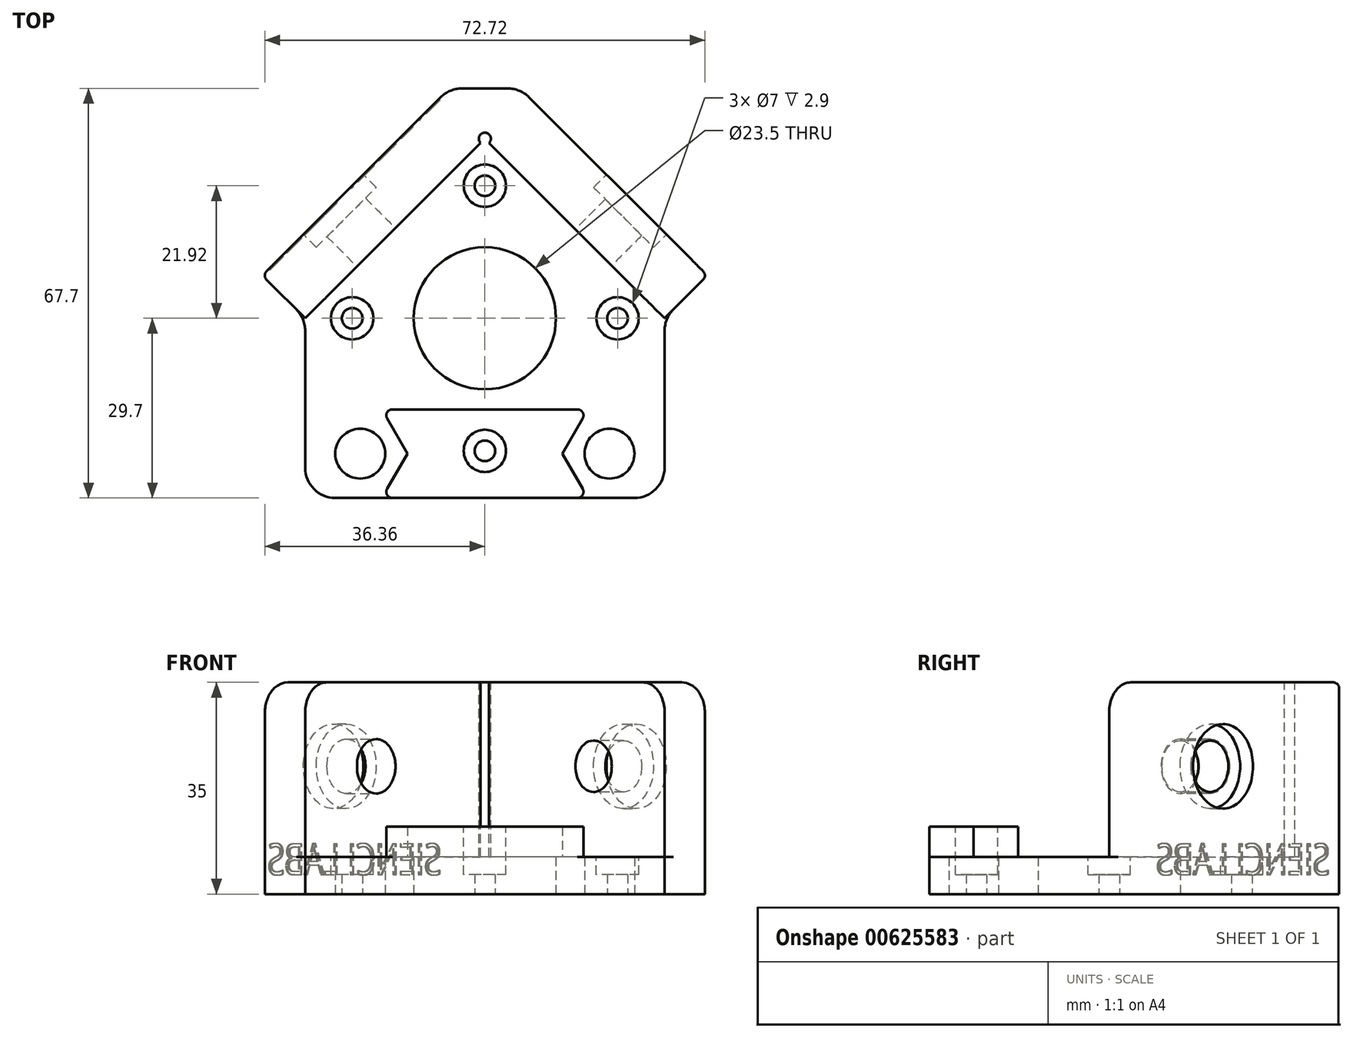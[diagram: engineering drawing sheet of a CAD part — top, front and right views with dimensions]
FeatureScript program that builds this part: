
annotation { "Feature Type Name" : "Feature", "Feature Type Description" : "" }
export const myFeature = defineFeature(function(context is Context, id is Id, definition is map)
    precondition{}
    {
        {
            var Q0;
            Q0=qCreatedBy(makeId("Top.planeOp"),FACE);
            var sketch = newSketch(context, id + "F0", { "sketchPlane" : qUnion([Q0])});
            skLineSegment(sketch, "E0", {"start": v(0, 0) * mm, "end": v(-29.7, 0) * mm});
            skLineSegment(sketch, "E1", {"start": v(-29.7, 0) * mm, "end": v(-29.7, 29.7) * mm});
            skLineSegment(sketch, "E2", {"start": v(-29.7, 29.7) * mm, "end": v(0, 59.4) * mm});
            skLineSegment(sketch, "E3", {"start": v(0, 59.4) * mm, "end": v(0, 0) * mm, "construction": true});
            skLineSegment(sketch, "E4", {"start": v(-29.7, 7.78) * mm, "end": v(0, 7.78) * mm, "construction": true});
            skCircle(sketch, "E5", {"center": v(0, 29.7) * mm, "radius": 11.75 * mm});
            skLineSegment(sketch, "E6", {"start": v(0, 29.7) * mm, "end": v(0, 59.4) * mm, "construction": true});
            skLineSegment(sketch, "E7", {"start": v(0, 59.4) * mm, "end": v(-29.7, 29.7) * mm, "construction": true});
            skLineSegment(sketch, "E8", {"start": v(-29.7, 29.7) * mm, "end": v(0, 0) * mm, "construction": true});
            skLineSegment(sketch, "E9", {"start": v(0, 51.62) * mm, "end": v(-21.92, 29.7) * mm, "construction": true});
            skLineSegment(sketch, "E10", {"start": v(-21.92, 29.7) * mm, "end": v(0, 7.78) * mm, "construction": true});
            skCircle(sketch, "E11", {"center": v(-20.59, 7.32) * mm, "radius": 4.12 * mm});
            skCircle(sketch, "E12", {"center": v(-21.92, 29.7) * mm, "radius": 1.7 * mm});
            skCircle(sketch, "E13", {"center": v(0, 51.62) * mm, "radius": 1.7 * mm});
            skCircle(sketch, "E14", {"center": v(0, 7.78) * mm, "radius": 1.7 * mm});
            skLineSegment(sketch, "E15.MirrorCS", {"start": v(29.7, 29.7) * mm, "end": v(0, 59.4) * mm});
            skLineSegment(sketch, "E16.MirrorCS", {"start": v(0, 0) * mm, "end": v(29.7, 0) * mm});
            skLineSegment(sketch, "E17.MirrorCS", {"start": v(29.7, 0) * mm, "end": v(29.7, 29.7) * mm});
            skLineSegment(sketch, "E18.MirrorCS", {"start": v(29.7, 7.78) * mm, "end": v(0, 7.78) * mm, "construction": true});
            skCircle(sketch, "E19.MirrorC", {"center": v(21.92, 29.7) * mm, "radius": 1.7 * mm});
            skCircle(sketch, "E20.MirrorC", {"center": v(20.6, 7.32) * mm, "radius": 4.12 * mm});
            skLineSegment(sketch, "E21.MirrorCS", {"start": v(0, 59.4) * mm, "end": v(29.7, 29.7) * mm, "construction": true});
            skLineSegment(sketch, "E22.MirrorCS", {"start": v(0, 51.62) * mm, "end": v(21.92, 29.7) * mm, "construction": true});
            skLineSegment(sketch, "E23.MirrorCS", {"start": v(21.92, 29.7) * mm, "end": v(0, 7.78) * mm, "construction": true});
            skLineSegment(sketch, "E24.MirrorCS", {"start": v(29.7, 29.7) * mm, "end": v(0, 0) * mm, "construction": true});
            skSolve(sketch);
        }
        {
            var Q0;
            Q0=qSketchRegion(id+"F0",true);
            extrude(context, id + "F1", {"entities" : qUnion([Q0]), "depth" : 6.13 * mm, "offsetDistance" : 25 * mm});
        }
        {
            var Q0;
            Q0=makeQuery(id+"F1.opExtrude","CAP_FACE",FACE,{"disambiguationData":[OSD([sQuery(id+"F0.wireOp",EDGE,"E0"),sQuery(id+"F0.wireOp",EDGE,"E1"),sQuery(id+"F0.wireOp",EDGE,"E2"),sQuery(id+"F0.wireOp",EDGE,"E5"),sQuery(id+"F0.wireOp",EDGE,"E11"),sQuery(id+"F0.wireOp",EDGE,"E12"),sQuery(id+"F0.wireOp",EDGE,"E15.MirrorCS"),sQuery(id+"F0.wireOp",EDGE,"E16.MirrorCS"),sQuery(id+"F0.wireOp",EDGE,"E17.MirrorCS"),sQuery(id+"F0.wireOp",EDGE,"E14"),sQuery(id+"F0.wireOp",EDGE,"E13"),sQuery(id+"F0.wireOp",EDGE,"E19.MirrorC"),sQuery(id+"F0.wireOp",EDGE,"E20.MirrorC")])],"isStart":true});
            var sketch = newSketch(context, id + "F2", { "sketchPlane" : qUnion([Q0])});
            skLineSegment(sketch, "E25", {"start": v(-29.7, -29.7) * mm, "end": v(-36.77, -36.77) * mm});
            skLineSegment(sketch, "E26", {"start": v(-36.77, -36.77) * mm, "end": v(-5.84, -67.7) * mm});
            skLineSegment(sketch, "E27", {"start": v(-5.84, -67.7) * mm, "end": v(0, -67.7) * mm});
            skLineSegment(sketch, "E28", {"start": v(0, -29.7) * mm, "end": v(-11.75, -29.7) * mm, "construction": true});
            skLineSegment(sketch, "E29", {"start": v(0, -67.7) * mm, "end": v(0, -29.7) * mm, "construction": true});
            skLineSegment(sketch, "E30.MirrorCS", {"start": v(0, -29.7) * mm, "end": v(11.75, -29.7) * mm, "construction": true});
            skLineSegment(sketch, "E31.MirrorCS", {"start": v(5.84, -67.7) * mm, "end": v(0, -67.7) * mm});
            skLineSegment(sketch, "E32.MirrorCS", {"start": v(36.77, -36.77) * mm, "end": v(5.84, -67.7) * mm});
            skLineSegment(sketch, "E33.MirrorCS", {"start": v(29.7, -29.7) * mm, "end": v(36.77, -36.77) * mm});
            skLineSegment(sketch, "E34", {"start": v(-29.7, -29.7) * mm, "end": v(0, -59.4) * mm});
            skLineSegment(sketch, "E35", {"start": v(0, -59.4) * mm, "end": v(29.7, -29.7) * mm});
            skSolve(sketch);
        }
        {
            var Q0;
            Q0=qSketchRegion(id+"F2",true);
            extrude(context, id + "F3", {"entities" : qUnion([Q0]), "operationType" : NewBodyOperationType.ADD, "oppositeDirection" : true, "depth" : 35 * mm, "offsetDistance" : 25 * mm});
        }
        {
            var Q0;
            Q0=makeQuery(id+"F3.opExtrude","SWEPT_FACE",FACE,{"disambiguationData":[OSD([sQuery(id+"F2.wireOp",EDGE,"E34")])]});
            var sketch = newSketch(context, id + "F4", { "sketchPlane" : qUnion([Q0])});
            skCircle(sketch, "E36", {"center": v(16.6, 21.13) * mm, "radius": 4.5 * mm});
            skLineSegment(sketch, "E37", {"start": v(42, 6.13) * mm, "end": v(-8.8, 6.13) * mm, "construction": true});
            skLineSegment(sketch, "E38", {"start": v(16.6, 6.13) * mm, "end": v(16.6, 35) * mm, "construction": true});
            skSolve(sketch);
        }
        {
            var Q0;
            Q0=qSketchRegion(id+"F4",true);
            extrude(context, id + "F5", {"entities" : qUnion([Q0]), "operationType" : NewBodyOperationType.REMOVE, "endBound" : BoundingType.UP_TO_NEXT, "oppositeDirection" : true, "depth" : 25 * mm, "offsetDistance" : 25 * mm});
        }
        {
            var Q0;
            Q0=makeQuery(id+"F3.opExtrude","SWEPT_FACE",FACE,{"disambiguationData":[OSD([sQuery(id+"F2.wireOp",EDGE,"E35")])]});
            var sketch = newSketch(context, id + "F6", { "sketchPlane" : qUnion([Q0])});
            skLineSegment(sketch, "E39", {"start": v(-42, 6.13) * mm, "end": v(8.8, 6.13) * mm, "construction": true});
            skLineSegment(sketch, "E40", {"start": v(-16.6, 6.13) * mm, "end": v(-16.6, 35) * mm, "construction": true});
            skCircle(sketch, "E41", {"center": v(-16.6, 21.13) * mm, "radius": 4.25 * mm});
            skSolve(sketch);
        }
        {
            var Q0;
            Q0=qSketchRegion(id+"F6",true);
            extrude(context, id + "F7", {"entities" : qUnion([Q0]), "operationType" : NewBodyOperationType.REMOVE, "endBound" : BoundingType.UP_TO_NEXT, "oppositeDirection" : true, "depth" : 25 * mm, "offsetDistance" : 25 * mm});
        }
        {
            var Q0;
            Q0=makeQuery(id+"F3.opExtrude","SWEPT_FACE",FACE,{"disambiguationData":[OSD([sQuery(id+"F2.wireOp",EDGE,"E26")])]});
            var sketch = newSketch(context, id + "F8", { "sketchPlane" : qUnion([Q0])});
            skCircle(sketch, "E42", {"center": v(-16.6, 21.13) * mm, "radius": 7 * mm});
            skSolve(sketch);
        }
        {
            var Q0;
            Q0=qSketchRegion(id+"F8",true);
            extrude(context, id + "F9", {"entities" : qUnion([Q0]), "operationType" : NewBodyOperationType.REMOVE, "oppositeDirection" : true, "depth" : 3 * mm, "offsetDistance" : 25 * mm});
        }
        {
            var Q0;
            Q0=makeQuery(id+"F3.opExtrude","SWEPT_FACE",FACE,{"disambiguationData":[OSD([sQuery(id+"F2.wireOp",EDGE,"E32.MirrorCS")])]});
            var sketch = newSketch(context, id + "F10", { "sketchPlane" : qUnion([Q0])});
            skCircle(sketch, "E43", {"center": v(16.6, 21.13) * mm, "radius": 7 * mm});
            skSolve(sketch);
        }
        {
            var Q0;
            Q0=qSketchRegion(id+"F10",true);
            extrude(context, id + "F11", {"entities" : qUnion([Q0]), "operationType" : NewBodyOperationType.REMOVE, "oppositeDirection" : true, "depth" : 3 * mm, "offsetDistance" : 25 * mm});
        }
        {
            var Q0;
            Q0=makeQuery(id+"F1.opExtrude","CAP_FACE",FACE,{"disambiguationData":[OSD([sQuery(id+"F0.wireOp",EDGE,"E0"),sQuery(id+"F0.wireOp",EDGE,"E1"),sQuery(id+"F0.wireOp",EDGE,"E2"),sQuery(id+"F0.wireOp",EDGE,"E5"),sQuery(id+"F0.wireOp",EDGE,"E11"),sQuery(id+"F0.wireOp",EDGE,"E12"),sQuery(id+"F0.wireOp",EDGE,"E15.MirrorCS"),sQuery(id+"F0.wireOp",EDGE,"E16.MirrorCS"),sQuery(id+"F0.wireOp",EDGE,"E17.MirrorCS"),sQuery(id+"F0.wireOp",EDGE,"E14"),sQuery(id+"F0.wireOp",EDGE,"E13"),sQuery(id+"F0.wireOp",EDGE,"E19.MirrorC"),sQuery(id+"F0.wireOp",EDGE,"E20.MirrorC")])],"isStart":false});
            var sketch = newSketch(context, id + "F12", { "sketchPlane" : qUnion([Q0])});
            skCircle(sketch, "E44", {"center": v(0, 51.62) * mm, "radius": 3.5 * mm});
            skCircle(sketch, "E45", {"center": v(-21.92, 29.7) * mm, "radius": 3.5 * mm});
            skCircle(sketch, "E46", {"center": v(21.92, 29.7) * mm, "radius": 3.5 * mm});
            skCircle(sketch, "E47", {"center": v(0, 7.78) * mm, "radius": 3.5 * mm});
            skSolve(sketch);
        }
        {
            var Q0;
            Q0=makeQuery(id+"F3.opExtrude","CAP_EDGE",EDGE,{"disambiguationData":[OSD([sQuery(id+"F2.wireOp",EDGE,"E33.MirrorCS")])],"isStart":false});
            var Q1;
            Q1=makeQuery(id+"F3.opExtrude","CAP_EDGE",EDGE,{"disambiguationData":[OSD([sQuery(id+"F2.wireOp",EDGE,"E25")])],"isStart":false});
            var Q2;
            {var subQ0=sQuery(id+"F0.wireOp",EDGE,"E17.MirrorCS");Q2=makeQuery(id+"F3.boolean.opBoolean","MERGE",EDGE,{"derivedFrom":[makeQuery(id+"F1.opExtrude","SWEPT_EDGE",EDGE,{"disambiguationData":[OSD([sQuery(id+"F0.wireOp",EDGE,"E15.MirrorCS"),subQ0])]}),makeQuery(id+"F3.opExtrude","SWEPT_EDGE",EDGE,{"disambiguationData":[OSD([subQ0,sQuery(id+"F2.wireOp",EDGE,"E33.MirrorCS"),sQuery(id+"F2.wireOp",EDGE,"E35")])]})]});}
            var Q3;
            Q3=makeQuery(id+"F1.opExtrude","SWEPT_EDGE",EDGE,{"disambiguationData":[OSD([sQuery(id+"F0.wireOp",EDGE,"E16.MirrorCS"),sQuery(id+"F0.wireOp",EDGE,"E17.MirrorCS")])]});
            var Q4;
            Q4=makeQuery(id+"F1.opExtrude","SWEPT_EDGE",EDGE,{"disambiguationData":[OSD([sQuery(id+"F0.wireOp",EDGE,"E0"),sQuery(id+"F0.wireOp",EDGE,"E1")])]});
            var Q5;
            {var subQ0=sQuery(id+"F0.wireOp",EDGE,"E1");Q5=makeQuery(id+"F3.boolean.opBoolean","MERGE",EDGE,{"derivedFrom":[makeQuery(id+"F1.opExtrude","SWEPT_EDGE",EDGE,{"disambiguationData":[OSD([subQ0,sQuery(id+"F0.wireOp",EDGE,"E2")])]}),makeQuery(id+"F3.opExtrude","SWEPT_EDGE",EDGE,{"disambiguationData":[OSD([subQ0,sQuery(id+"F2.wireOp",EDGE,"E25"),sQuery(id+"F2.wireOp",EDGE,"E34")])]})]});}
            var Q6;
            Q6=makeQuery(id+"F3.opExtrude","SWEPT_EDGE",EDGE,{"disambiguationData":[OSD([sQuery(id+"F2.wireOp",EDGE,"E26"),sQuery(id+"F2.wireOp",EDGE,"E27")])]});
            var Q7;
            Q7=makeQuery(id+"F3.opExtrude","SWEPT_EDGE",EDGE,{"disambiguationData":[OSD([sQuery(id+"F2.wireOp",EDGE,"E31.MirrorCS"),sQuery(id+"F2.wireOp",EDGE,"E32.MirrorCS")])]});
            fillet(context, id + "F13", {"entities" : qUnion([Q0, Q1, Q2, Q3, Q4, Q5, Q6, Q7]), "radius" : 5 * mm, "tangentPropagation" : true, "allowEdgeOverflow" : false});
        }
        {
            var Q0;
            Q0=qSketchRegion(id+"F12",true);
            extrude(context, id + "F14", {"entities" : qUnion([Q0]), "operationType" : NewBodyOperationType.REMOVE, "oppositeDirection" : true, "depth" : 2.9 * mm, "offsetDistance" : 25 * mm});
        }
        {
            var Q0;
            Q0=makeQuery(id+"F3.opExtrude","SWEPT_FACE",FACE,{"disambiguationData":[OSD([sQuery(id+"F2.wireOp",EDGE,"E26")])]});
            var sketch = newSketch(context, id + "F15", { "sketchPlane" : qUnion([Q0])});
            skText(sketch, "E48", { "text": "SIENCI LABS\n", "fontName": "OpenSans-Regular.ttf"});
            const initialGuessF15  = {"E48": [-0.04167, 0.0032, 1, 0, 0.00516]};
            skSetInitialGuess(sketch, initialGuessF15);
            skSolve(sketch);
        }
        {
            var Q0;
            Q0=qSketchRegion(id+"F15",true);
            extrude(context, id + "F16", {"entities" : qUnion([Q0]), "operationType" : NewBodyOperationType.REMOVE, "oppositeDirection" : true, "depth" : 0.25 * mm, "offsetDistance" : 25 * mm});
        }
        {
            var Q0;
            Q0=makeQuery(id+"F1.opExtrude","CAP_FACE",FACE,{"disambiguationData":[OSD([sQuery(id+"F0.wireOp",EDGE,"E0"),sQuery(id+"F0.wireOp",EDGE,"E1"),sQuery(id+"F0.wireOp",EDGE,"E2"),sQuery(id+"F0.wireOp",EDGE,"E5"),sQuery(id+"F0.wireOp",EDGE,"E11"),sQuery(id+"F0.wireOp",EDGE,"E12"),sQuery(id+"F0.wireOp",EDGE,"E15.MirrorCS"),sQuery(id+"F0.wireOp",EDGE,"E16.MirrorCS"),sQuery(id+"F0.wireOp",EDGE,"E17.MirrorCS"),sQuery(id+"F0.wireOp",EDGE,"E14"),sQuery(id+"F0.wireOp",EDGE,"E13"),sQuery(id+"F0.wireOp",EDGE,"E19.MirrorC"),sQuery(id+"F0.wireOp",EDGE,"E20.MirrorC")])],"isStart":false});
            var sketch = newSketch(context, id + "F17", { "sketchPlane" : qUnion([Q0])});
            skCircle(sketch, "E49.cCircle", {"center": v(-20.59, 7.32) * mm, "radius": 6.75 * mm, "construction": true});
            skLineSegment(sketch, "E49.0", {"start": v(-16.7, 14.07) * mm, "end": v(-12.8, 7.32) * mm});
            skLineSegment(sketch, "E49.1", {"start": v(-12.8, 7.32) * mm, "end": v(-16.7, 0.57) * mm});
            skLineSegment(sketch, "E49.2", {"start": v(-16.7, 0.57) * mm, "end": v(-24.49, 0.57) * mm});
            skLineSegment(sketch, "E49.3", {"start": v(-24.49, 0.57) * mm, "end": v(-28.38, 7.32) * mm});
            skLineSegment(sketch, "E49.4", {"start": v(-28.38, 7.32) * mm, "end": v(-24.49, 14.07) * mm});
            skLineSegment(sketch, "E49.5", {"start": v(-24.49, 14.07) * mm, "end": v(-16.7, 14.07) * mm});
            skPoint(sketch, "E49.0.midPoint", {"position": v(-14.74, 10.7) * mm});
            skLineSegment(sketch, "E50", {"start": v(0, 59.4) * mm, "end": v(0, 0) * mm, "construction": true});
            skLineSegment(sketch, "E51.MirrorCS", {"start": v(24.49, 14.07) * mm, "end": v(16.7, 14.07) * mm});
            skLineSegment(sketch, "E52.MirrorCS", {"start": v(16.7, 14.07) * mm, "end": v(12.8, 7.32) * mm});
            skLineSegment(sketch, "E53.MirrorCS", {"start": v(28.38, 7.32) * mm, "end": v(24.49, 14.07) * mm});
            skCircle(sketch, "E54.MirrorC", {"center": v(20.59, 7.32) * mm, "radius": 6.75 * mm, "construction": true});
            skLineSegment(sketch, "E55.MirrorCS", {"start": v(24.49, 0.57) * mm, "end": v(28.38, 7.32) * mm});
            skLineSegment(sketch, "E56.MirrorCS", {"start": v(12.8, 7.32) * mm, "end": v(16.7, 0.57) * mm});
            skLineSegment(sketch, "E57.MirrorCS", {"start": v(16.7, 0.57) * mm, "end": v(24.49, 0.57) * mm});
            skPoint(sketch, "E58.MirrorP", {"position": v(14.74, 10.7) * mm});
            skLineSegment(sketch, "E59", {"start": v(-16.7, 14.07) * mm, "end": v(16.7, 14.07) * mm});
            skLineSegment(sketch, "E60", {"start": v(-16.7, 0.57) * mm, "end": v(16.7, 0.57) * mm});
            skCircle(sketch, "E61", {"center": v(0, 7.78) * mm, "radius": 3.5 * mm});
            skLineSegment(sketch, "E62", {"start": v(-16.7, 0.57) * mm, "end": v(-17.02, 0) * mm});
            skLineSegment(sketch, "E63", {"start": v(-17.02, 0) * mm, "end": v(0, 0) * mm});
            skLineSegment(sketch, "E64.MirrorCS", {"start": v(16.7, 0.57) * mm, "end": v(17.02, 0) * mm});
            skLineSegment(sketch, "E65.MirrorCS", {"start": v(17.02, 0) * mm, "end": v(0, 0) * mm});
            skLineSegment(sketch, "E66", {"start": v(-12.8, 7.32) * mm, "end": v(12.8, 7.32) * mm, "construction": true});
            skLineSegment(sketch, "E67.MirrorCS", {"start": v(-16.7, 14.07) * mm, "end": v(-17.02, 14.64) * mm});
            skLineSegment(sketch, "E68.MirrorCS", {"start": v(16.7, 14.07) * mm, "end": v(17.02, 14.64) * mm});
            skLineSegment(sketch, "E69.MirrorCS", {"start": v(-17.02, 14.64) * mm, "end": v(0, 14.64) * mm});
            skLineSegment(sketch, "E70.MirrorCS", {"start": v(17.02, 14.64) * mm, "end": v(0, 14.64) * mm});
            skSolve(sketch);
        }
        {
            var Q0;
            Q0=makeQuery(id+"F17.imprint","IMPRINT",FACE,{"disambiguationData":[TD([[makeQuery(id+"F17.imprint","IMPRINT",EDGE,{"derivedFrom":sQuery(id+"F17.wireOp",EDGE,"E49.0")}),1.0]])]});
            var Q1;
            Q1=makeQuery(id+"F17.imprint","IMPRINT",FACE,{"disambiguationData":[TD([[makeQuery(id+"F17.imprint","IMPRINT",EDGE,{"derivedFrom":sQuery(id+"F17.wireOp",EDGE,"E60")}),-1.0]])]});
            var Q2;
            Q2=makeQuery(id+"F17.imprint","IMPRINT",FACE,{"disambiguationData":[TD([[makeQuery(id+"F17.imprint","IMPRINT",EDGE,{"derivedFrom":sQuery(id+"F17.wireOp",EDGE,"E67.MirrorCS")}),-1.0]])]});
            extrude(context, id + "F18", {"entities" : qUnion([Q0, Q1, Q2]), "operationType" : NewBodyOperationType.ADD, "depth" : 5 * mm, "offsetDistance" : 25 * mm});
        }
        {
            var Q0;
            Q0=makeQuery(id+"F3.opExtrude","SWEPT_EDGE",EDGE,{"disambiguationData":[OSD([sQuery(id+"F2.wireOp",EDGE,"E32.MirrorCS"),sQuery(id+"F2.wireOp",EDGE,"E33.MirrorCS")])]});
            var Q1;
            Q1=makeQuery(id+"F18.opExtrude","SWEPT_EDGE",EDGE,{"disambiguationData":[OSD([sQuery(id+"F0.wireOp",EDGE,"E0"),sQuery(id+"F0.wireOp",EDGE,"E16.MirrorCS"),sQuery(id+"F17.wireOp",EDGE,"E62"),sQuery(id+"F17.wireOp",EDGE,"E63")])]});
            var Q2;
            Q2=makeQuery(id+"F18.opExtrude","SWEPT_EDGE",EDGE,{"disambiguationData":[OSD([sQuery(id+"F17.wireOp",EDGE,"E67.MirrorCS"),sQuery(id+"F17.wireOp",EDGE,"E69.MirrorCS")])]});
            var Q3;
            Q3=makeQuery(id+"F18.opExtrude","SWEPT_EDGE",EDGE,{"disambiguationData":[OSD([sQuery(id+"F17.wireOp",EDGE,"E68.MirrorCS"),sQuery(id+"F17.wireOp",EDGE,"E70.MirrorCS")])]});
            var Q4;
            Q4=makeQuery(id+"F18.opExtrude","SWEPT_EDGE",EDGE,{"disambiguationData":[OSD([sQuery(id+"F0.wireOp",EDGE,"E0"),sQuery(id+"F0.wireOp",EDGE,"E16.MirrorCS"),sQuery(id+"F17.wireOp",EDGE,"E64.MirrorCS"),sQuery(id+"F17.wireOp",EDGE,"E65.MirrorCS")])]});
            fillet(context, id + "F19", {"entities" : qUnion([Q0, Q1, Q2, Q3, Q4]), "radius" : 1 * mm, "tangentPropagation" : true, "allowEdgeOverflow" : false});
        }
        {
            var Q0;
            Q0=makeQuery(id+"F3.opExtrude","CAP_FACE",FACE,{"disambiguationData":[OSD([sQuery(id+"F2.wireOp",EDGE,"E25"),sQuery(id+"F2.wireOp",EDGE,"E26"),sQuery(id+"F2.wireOp",EDGE,"E27"),sQuery(id+"F2.wireOp",EDGE,"E31.MirrorCS"),sQuery(id+"F2.wireOp",EDGE,"E32.MirrorCS"),sQuery(id+"F2.wireOp",EDGE,"E33.MirrorCS"),sQuery(id+"F2.wireOp",EDGE,"E34"),sQuery(id+"F2.wireOp",EDGE,"E35")])],"isStart":false});
            var sketch = newSketch(context, id + "F20", { "sketchPlane" : qUnion([Q0])});
            skCircle(sketch, "E71", {"center": v(0, 59.4) * mm, "radius": 1 * mm});
            skSolve(sketch);
        }
        {
            var Q0;
            Q0=qSketchRegion(id+"F20",true);
            var Q1;
            Q1=makeQuery(id+"F1.opExtrude","CAP_FACE",FACE,{"disambiguationData":[OSD([sQuery(id+"F0.wireOp",EDGE,"E0"),sQuery(id+"F0.wireOp",EDGE,"E1"),sQuery(id+"F0.wireOp",EDGE,"E2"),sQuery(id+"F0.wireOp",EDGE,"E5"),sQuery(id+"F0.wireOp",EDGE,"E11"),sQuery(id+"F0.wireOp",EDGE,"E12"),sQuery(id+"F0.wireOp",EDGE,"E15.MirrorCS"),sQuery(id+"F0.wireOp",EDGE,"E16.MirrorCS"),sQuery(id+"F0.wireOp",EDGE,"E17.MirrorCS"),sQuery(id+"F0.wireOp",EDGE,"E14"),sQuery(id+"F0.wireOp",EDGE,"E13"),sQuery(id+"F0.wireOp",EDGE,"E19.MirrorC"),sQuery(id+"F0.wireOp",EDGE,"E20.MirrorC")])],"isStart":false});
            extrude(context, id + "F21", {"entities" : qUnion([Q0]), "operationType" : NewBodyOperationType.REMOVE, "endBound" : BoundingType.UP_TO_SURFACE, "oppositeDirection" : true, "depth" : 25 * mm, "endBoundEntityFace" : qUnion([Q1]), "offsetDistance" : 25 * mm});
        }
    });
